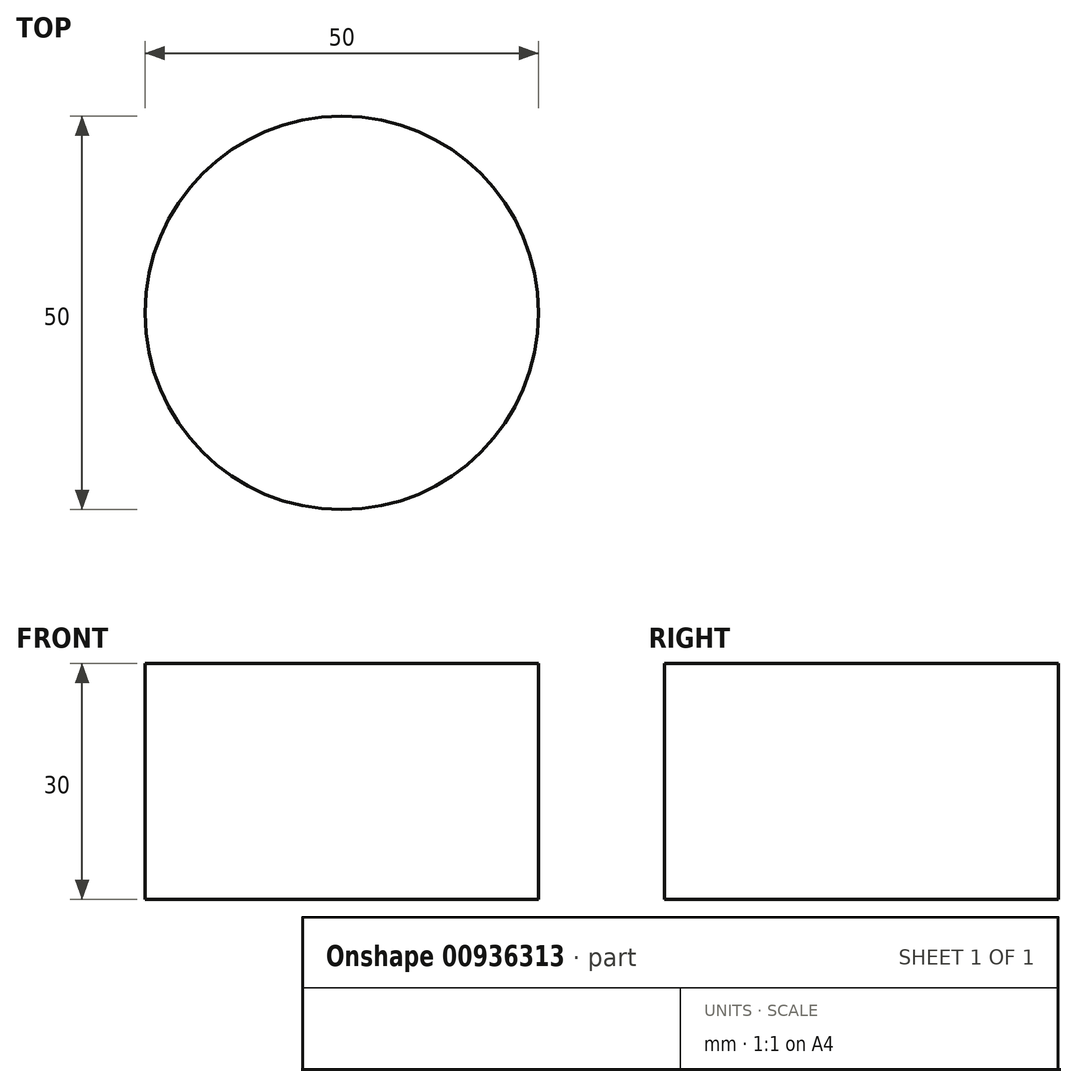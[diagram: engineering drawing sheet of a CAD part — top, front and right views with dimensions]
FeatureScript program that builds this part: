
annotation { "Feature Type Name" : "Feature", "Feature Type Description" : "" }
export const myFeature = defineFeature(function(context is Context, id is Id, definition is map)
    precondition{}
    {
        {
            var Q0;
            Q0=qCreatedBy(makeId("Right.planeOp"),FACE);
            var sketch = newSketch(context, id + "F0", { "sketchPlane" : qUnion([Q0])});
            skLineSegment(sketch, "E0.bottom", {"start": v(0, 0) * mm, "end": v(25, 0) * mm});
            skLineSegment(sketch, "E0.top", {"start": v(0, 30) * mm, "end": v(25, 30) * mm});
            skLineSegment(sketch, "E0.left", {"start": v(0, 0) * mm, "end": v(0, 30) * mm});
            skLineSegment(sketch, "E0.right", {"start": v(25, 0) * mm, "end": v(25, 30) * mm});
            skSolve(sketch);
        }
        {
            var Q0;
            Q0=makeQuery(id+"F0.imprint","IMPRINT",FACE,{"disambiguationData":[TD([[makeQuery(id+"F0.imprint","IMPRINT",EDGE,{"derivedFrom":sQuery(id+"F0.wireOp",EDGE,"E0.bottom")}),1.0]])]});
            var Q1;
            Q1=sQuery(id+"F0.wireOp",EDGE,"E0.left");
            revolve(context, id + "F1", {"surfaceOperationType" : NewSurfaceOperationType.NEW, "entities" : qUnion([Q0]), "axis" : qUnion([Q1]), "revolveType" : RevolveType.FULL});
        }
    });
